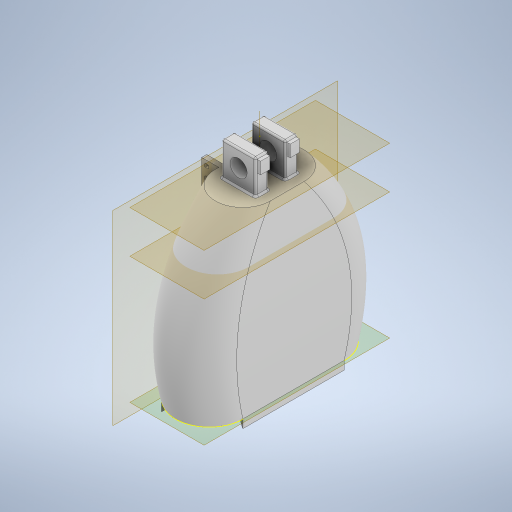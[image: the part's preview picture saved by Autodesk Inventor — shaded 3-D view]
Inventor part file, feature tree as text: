
AUTODESK INVENTOR PART (.ipt)
format: ipt  version: 2023 (Build 270158000, 158)  size: 826,880 bytes
history: native  units: mm
features: sketch x29, extrude x13, plane x4, fillet x3, chamfer x2, mirror x2, loft x1, shell x1, projected_geometry x1
ambient origin geometry x8: Origin, YZ Plane, XZ Plane, XY Plane, X Axis, Y Axis, Z Axis, Center Point
bodies: Solid1 (feature_tree)
feature tree (56):
  sketch  "Sketch1"  dims[d0=120.0mm d1=80.0mm d2=20.0mm]
  plane  "Work Plane1"
  sketch  "Sketch2"  dims[d3=200.0mm d4=40.0mm]
  plane  "Work Plane2"
  sketch  "Sketch3"  dims[d5=65.0mm d6=150.0mm]
  plane  "Work Plane3"
  loft  "Loft1"
  shell  "Shell1"  Thickness=20.0mm
  sketch  "Sketch4"  dims[d7=100.0mm d8=75.0mm]
  plane  "Work Plane4"
  extrude  "Extrusion1"  Depth=40.0mm
  sketch  "Sketch10"  dims[d15=3.0mm]
  extrude  "Extrusion2"  Depth=150.0mm
  sketch  "Sketch12"  dims[d22=40.0mm]
  extrude  "Extrusion3"  Depth=75.0mm
  extrude  "Extrusion4"  TaperAngle=0.0deg  [1 undecoded]
  fillet  "Fillet1"  [1 undecoded]
  chamfer  "Chamfer1"  Distance=10.0mm
  chamfer  "Chamfer2"  Distance=40.0mm
  extrude  "Extrusion5"  Depth=50.0mm TaperAngle=0.0deg
  extrude  "Extrusion7"  Depth=40.0mm TaperAngle=0.0deg
  mirror  "Mirror2"
  mirror  "Mirror3"
  sketch  "Sketch18"  dims[d36=2.0mm d37=2.0mm d38=45.0deg d39=55.0mm]
  sketch  "Sketch19"  dims[d40=25.0mm d41=12.5mm]
  extrude  "Extrusion8"  Depth=2.0mm TaperAngle=45.0deg
  fillet  "Fillet2"  Radius=55.0mm
  sketch  "Sketch21"  dims[d44=2.0mm d45=2.0mm]
  sketch  "Sketch22"  dims[d46=10.0mm d47=0.0mm d55=4.0mm]
  sketch  "Sketch23"  dims[d56=5.0mm d57=5.0mm d58=50.0mm d59=0.0mm]
  sketch  "Sketch24"  dims[d60=3.0mm d61=10.0mm d62=0.0mm]
  sketch  "Sketch25"  dims[d63=20.0mm]
  sketch  "Sketch26"  dims[d64=50.0mm]
  sketch  "Sketch27"  dims[d65=129.0mm]
  sketch  "Sketch28"  dims[d66=50.0mm]
  extrude  "Extrusion9"  Depth=12.5mm
  extrude  "Extrusion10"  Depth=5.0mm
  extrude  "Extrusion11"  Depth=2.0mm
  extrude  "Extrusion12"  Depth=4.0mm
  extrude  "Extrusion13"  Depth=5.0mm
  fillet  "Fillet3"  Radius=50.0mm
  extrude  "Extrusion14"  Depth=10.0mm TaperAngle=0.0deg
  sketch  "Sketch34"  dims[d73=9.0mm d74=0.0mm d75=12.0mm d76=0.0mm d77=12.0mm d78=4.0mm d79=4.0mm d80=4.0mm d81=9.0mm d82=4.0mm d83=9.0mm d84=4.0mm d85=9.0mm d86=4.0mm d87=40.0mm d88=0.0mm d89=11.0mm d90=4.0mm d91=4.0mm d92=0.0mm d93=2.0mm d94=10.0mm d95=0.0mm]
  sketch  "Sketch9"  dims[d9=0.0mm d10=90.0deg d11=0.0mm d12=90.0deg d13=0.0mm d14=90.0deg]
  projected_geometry  "Projected Loop1"
  sketch  "Sketch11"  dims[d19=21.0mm d20=10.0mm d21=0.0mm]
  sketch  "Sketch13"  dims[d23=50.0mm d24=40.0mm d25=0.0mm]
  sketch  "Sketch14"  dims[d26=20.0mm d27=50.0mm d28=0.0mm]
  sketch  "Sketch15"  dims[d29=20.0mm d30=40.0mm d31=0.0mm]
  sketch  "Sketch17"  dims[d32=2.0mm d33=2.0mm d34=2.0mm d35=45.0deg]
  sketch  "Sketch20"  dims[d42=5.0mm d43=5.0mm]
  sketch  "Sketch29"  dims[d67=6.0mm]
  sketch  "Sketch30"  dims[d68=6.0mm]
  sketch  "Sketch31"  dims[d69=10.0mm d70=0.0mm]
  sketch  "Sketch32"  dims[d71=6.0mm]
  sketch  "Sketch33"  dims[d72=6.0mm]
note: 2 required parameter values undecoded (feature->parameter linkage not recoverable at this tier; creation-order binding heuristic only, values carry confidence <= 0.55)
